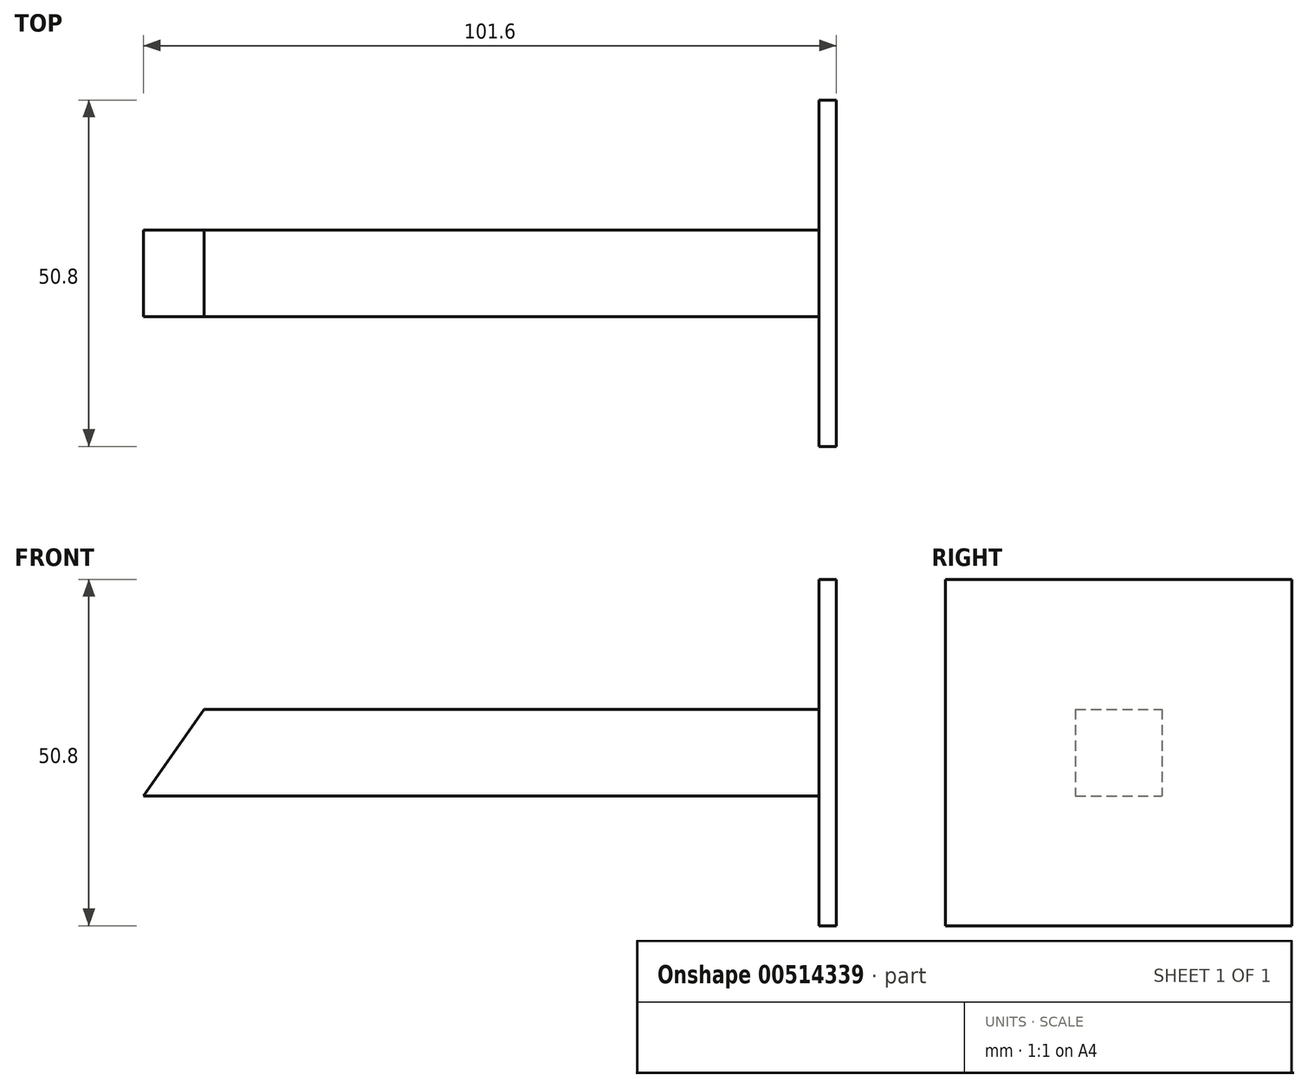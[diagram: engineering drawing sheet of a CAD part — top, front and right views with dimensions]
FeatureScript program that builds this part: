
annotation { "Feature Type Name" : "Feature", "Feature Type Description" : "" }
export const myFeature = defineFeature(function(context is Context, id is Id, definition is map)
    precondition{}
    {
        {
            var Q0;
            Q0=qCreatedBy(makeId("Front.planeOp"),FACE);
            var sketch = newSketch(context, id + "F0", { "sketchPlane" : qUnion([Q0])});
            skLineSegment(sketch, "E0.bottom", {"start": v(-43.13, 20.81) * mm, "end": v(58.47, 20.81) * mm});
            skLineSegment(sketch, "E0.top", {"start": v(-43.13, 8.11) * mm, "end": v(58.47, 8.11) * mm});
            skLineSegment(sketch, "E0.left", {"start": v(-43.13, 20.81) * mm, "end": v(-43.13, 8.11) * mm});
            skLineSegment(sketch, "E0.right", {"start": v(58.47, 20.81) * mm, "end": v(58.47, 8.11) * mm});
            skSolve(sketch);
        }
        {
            var Q0;
            Q0=makeQuery(id+"F0.imprint","IMPRINT",FACE,{"disambiguationData":[TD([[makeQuery(id+"F0.imprint","IMPRINT",EDGE,{"derivedFrom":sQuery(id+"F0.wireOp",EDGE,"E0.bottom")}),-1.0]])]});
            extrude(context, id + "F1", {"entities" : qUnion([Q0]), "depth" : 12.7 * mm});
        }
        {
            var Q0;
            Q0=makeQuery(id+"F1.opExtrude","CAP_FACE",FACE,{"disambiguationData":[OSD([sQuery(id+"F0.wireOp",EDGE,"E0.bottom"),sQuery(id+"F0.wireOp",EDGE,"E0.top"),sQuery(id+"F0.wireOp",EDGE,"E0.left"),sQuery(id+"F0.wireOp",EDGE,"E0.right")])],"isStart":false});
            var sketch = newSketch(context, id + "F2", { "sketchPlane" : qUnion([Q0])});
            skLineSegment(sketch, "E1", {"start": v(-43.13, 8.11) * mm, "end": v(-34.24, 20.81) * mm});
            skLineSegment(sketch, "E2", {"start": v(-34.24, 20.81) * mm, "end": v(-43.13, 20.81) * mm});
            skLineSegment(sketch, "E3", {"start": v(-43.13, 20.81) * mm, "end": v(-43.13, 8.11) * mm});
            skSolve(sketch);
        }
        {
            var Q0;
            Q0 = qSketchRegion(id + "F2", true);
            extrude(context, id + "F3", {"entities" : qUnion([Q0]), "operationType" : NewBodyOperationType.REMOVE, "oppositeDirection" : true, "depth" : 25.4 * mm});
        }
        {
            var Q0;
            Q0=makeQuery(id+"F1.opExtrude","SWEPT_FACE",FACE,{"disambiguationData":[OSD([sQuery(id+"F0.wireOp",EDGE,"E0.right")])]});
            var sketch = newSketch(context, id + "F4", { "sketchPlane" : qUnion([Q0])});
            skSolve(sketch);
        }
        {
            var Q0;
            Q0 = qSketchRegion(id + "F4", true);
            var Q1;
            {var subQ0=sQuery(id+"F0.wireOp",EDGE,"E0.right");Q1=makeQuery(id+"F4.imprint","IMPRINT",FACE,{"disambiguationData":[TD([[makeQuery(id+"F4.imprint","IMPRINT",EDGE,{"derivedFrom":makeQuery(id+"F1.opExtrude","CAP_EDGE",EDGE,{"disambiguationData":[OSD([subQ0])],"isStart":true})}),-1.0]])]});}
            extrude(context, id + "F5", {"entities" : qUnion([Q0, Q1]), "operationType" : NewBodyOperationType.REMOVE, "oppositeDirection" : true, "depth" : 2.54 * mm});
        }
        {
            var Q0;
            Q0=makeQuery(id+"F5.boolean.opBoolean","COPY",FACE,{"derivedFrom":makeQuery(id+"F5.opExtrude","CAP_FACE",FACE,{"disambiguationData":[OSD([sQuery(id+"F0.wireOp",EDGE,"E0.bottom"),sQuery(id+"F0.wireOp",EDGE,"E0.top"),sQuery(id+"F0.wireOp",EDGE,"E0.right")])],"isStart":false})});
            var sketch = newSketch(context, id + "F6", { "sketchPlane" : qUnion([Q0])});
            skLineSegment(sketch, "E4", {"start": v(-31.75, 20.81) * mm, "end": v(-31.75, 39.86) * mm});
            skLineSegment(sketch, "E5.bottom", {"start": v(-31.75, 39.86) * mm, "end": v(19.05, 39.86) * mm});
            skLineSegment(sketch, "E5.top", {"start": v(-31.75, -10.94) * mm, "end": v(19.05, -10.94) * mm});
            skLineSegment(sketch, "E5.left", {"start": v(-31.75, 39.86) * mm, "end": v(-31.75, -10.94) * mm});
            skLineSegment(sketch, "E5.right", {"start": v(19.05, 39.86) * mm, "end": v(19.05, -10.94) * mm});
            skSolve(sketch);
        }
        {
            var Q0;
            Q0 = qSketchRegion(id + "F6", true);
            extrude(context, id + "F7", {"entities" : qUnion([Q0]), "operationType" : NewBodyOperationType.ADD, "depth" : 2.54 * mm});
        }
    });
